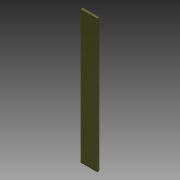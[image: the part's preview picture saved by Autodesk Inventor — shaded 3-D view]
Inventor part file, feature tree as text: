
AUTODESK INVENTOR PART (.ipt)
format: ipt  version: 2013 (Build 170138000, 138)  size: 68,096 bytes
history: native  units: in
note: dims shown in document units (in); Inventor stores cm internally (conversion verified against a paired STEP export)
features: extrude x1, sketch x1
ambient origin geometry x8: Origin, YZ Plane, XZ Plane, XY Plane, X Axis, Y Axis, Z Axis, Center Point
bodies: Solid1 (feature_tree)
feature tree (2):
  extrude  "Extrusion1"  Depth=2.0in
  sketch  "Sketch1"  dims[d0=16.0in d1=2.0in d2=0.25in d3=0.0in]
